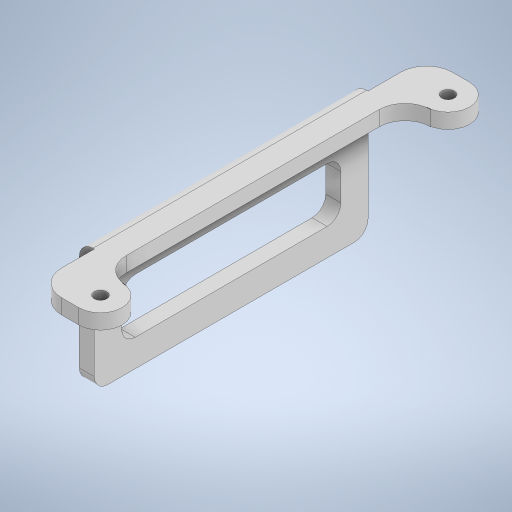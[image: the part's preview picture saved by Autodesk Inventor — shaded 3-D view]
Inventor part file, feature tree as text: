
AUTODESK INVENTOR PART (.ipt)
format: ipt  version: 2023 (Build 270158000, 158)  size: 306,688 bytes
history: native  units: in
note: dims shown in document units (in); Inventor stores cm internally (conversion verified against a paired STEP export)
features: extrude x3, sketch x3, fillet x1
ambient origin geometry x8: Origin, YZ Plane, XZ Plane, XY Plane, X Axis, Y Axis, Z Axis, Center Point
bodies: Solid1 (feature_tree)
feature tree (7):
  extrude  "Extrusion1"  Depth=0.116in
  extrude  "Extrusion2"  Depth=0.395in
  extrude  "Extrusion3"  Depth=0.395in
  fillet  "Fillet1"  Radius=0.2362in
  sketch  "Sketch1"  dims[d0=0.116in d2=0.116in]
  sketch  "Sketch2"  dims[d3=0.395in d4=0.395in]
  sketch  "Sketch4"  dims[d7=3.187in d8=0.395in d9=0.2362in d10=0.2362in d11=0.2362in d12=0.2362in d13=0.1378in d14=0.0in d15=0.3in d16=1.0in d17=2.51in d19=0.25in d22=0.125in d23=0.125in d24=0.125in d25=0.125in d26=0.125in d27=0.125in d28=0.1378in d29=0.0in d30=0.1378in d31=0.0in d32=0.125in d33=1.76in d34=1.76in]
